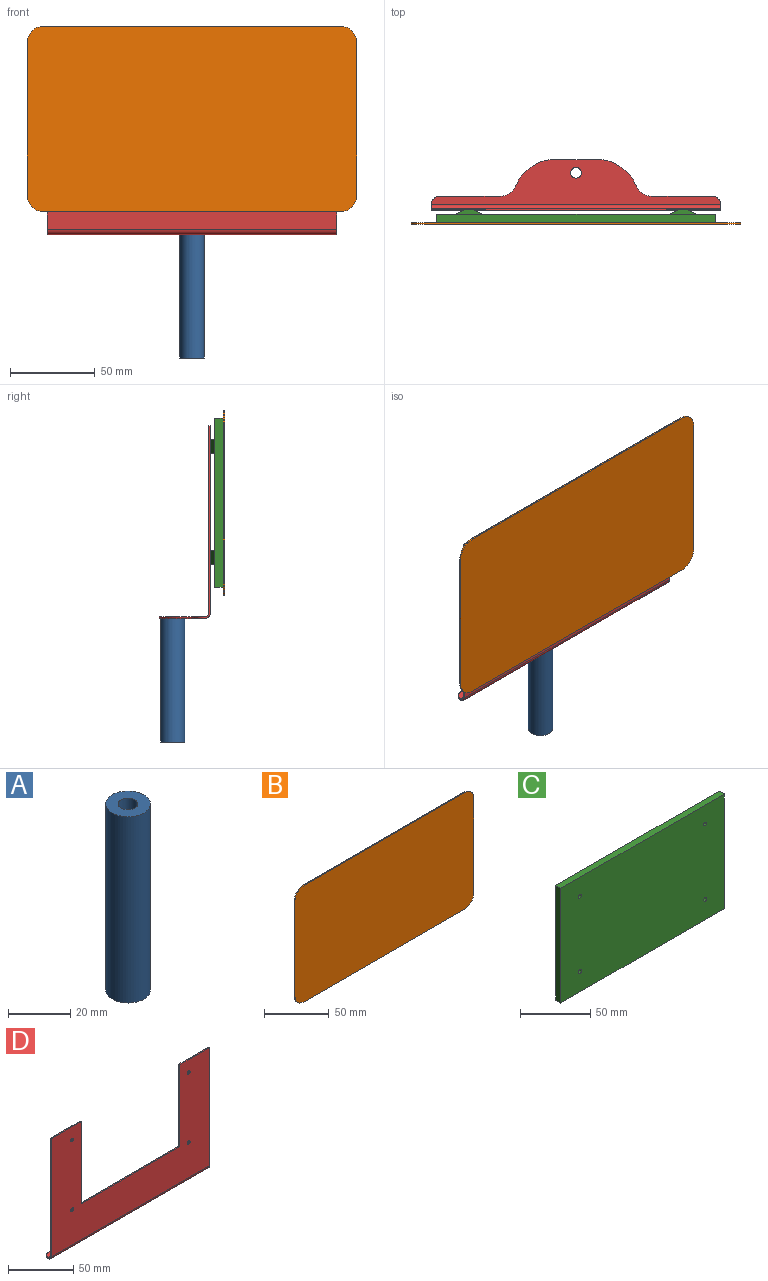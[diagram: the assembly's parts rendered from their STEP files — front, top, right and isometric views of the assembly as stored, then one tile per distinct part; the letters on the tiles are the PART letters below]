
ASSEMBLY  parts=4 mates=3
PART A: 4 faces, bbox 14.3x14.3x73 mm
  f0: cylinder r=3.17mm len=73mm, axis (0,0,1), area 1456.3mm2, adj f2,f3
  f1: cylinder r=7.15mm len=73mm, axis (0,0,1), area 3279.5mm2, adj f2,f3
  f2: plane 14.3x14.3mm, normal (0,0,-1), area 128.9mm2, adj f0,f1
  f3: plane 14.3x14.3mm, normal (0,0,1), area 128.9mm2, adj f0,f1
PART B: 10 faces, bbox 195x0.8x110 mm
  f0: plane 175x0.75mm, normal (0,0,-1), area 131.2mm2, adj f1,f7,f8,f9
  f1: cylinder r=10mm len=10mm, axis (0,1,0), area 11.8mm2, adj f0,f2,f8,f9
  f2: plane 90x0.75mm, normal (1,0,0), area 67.5mm2, adj f1,f3,f8,f9
  f3: cylinder r=10mm len=10mm, axis (0,1,0), area 11.8mm2, adj f2,f4,f8,f9
  f4: plane 175x0.75mm, normal (0,0,1), area 131.2mm2, adj f3,f5,f8,f9
  f5: cylinder r=10mm len=10mm, axis (0,1,0), area 11.8mm2, adj f4,f6,f8,f9
  f6: plane 90x0.75mm, normal (-1,0,0), area 67.5mm2, adj f5,f7,f8,f9
  f7: cylinder r=10mm len=10mm, axis (0,1,0), area 11.8mm2, adj f0,f6,f8,f9
  f8: plane 195x110mm, normal (0,-1,0), area 21364.2mm2, adj f0,f1,f2,f3,f4,f5,f6,f7
  f9: plane 195x110mm, normal (0,1,0), area 21364.2mm2, adj f0,f1,f2,f3,f4,f5,f6,f7
PART C: 30 faces, bbox 165x7.7x100 mm
  f0: plane 100x5.21mm, normal (-1,0,0), area 521mm2, adj f1,f6,f8,f9
  f1: plane 165x5.21mm, normal (0,0,-1), area 859.6mm2, adj f0,f2,f8,f9
  f2: plane 100x5.21mm, normal (1,0,0), area 521mm2, adj f1,f6,f8,f9
  f3: cylinder r=1.5mm len=7.71mm, axis (0,-1,0), area 72.7mm2, adj f9,f24
  f4: cylinder r=1.5mm len=7.71mm, axis (0,-1,0), area 72.7mm2, adj f9,f19
  f5: cylinder r=1.5mm len=7.71mm, axis (0,-1,0), area 72.7mm2, adj f9,f14
  f6: plane 165x5.21mm, normal (0,0,1), area 859.6mm2, adj f0,f2,f8,f9
  f7: cylinder r=1.5mm len=7.71mm, axis (0,-1,0), area 72.7mm2, adj f9,f29
  f8: plane 165x100mm, normal (0,1,0), area 15975.1mm2, adj f0,f1,f2,f6,f10,f11,f12,f13
  f9: plane 165x100mm, normal (0,-1,0), area 16471.7mm2, adj f0,f1,f2,f3,f4,f5,f6,f7
  f10: plane 8.15x5.36mm, normal (-0.42,0.91,0), area 48.2mm2, adj f8,f11,f13,f14
  f11: plane 16.1x2.5mm, normal (0,0,-1), area 26.8mm2, adj f8,f10,f12,f14
  f12: plane 8.15x5.36mm, normal (0.42,0.91,0), area 48.2mm2, adj f8,f11,f13,f14
  f13: plane 16.1x2.5mm, normal (0,0,1), area 26.8mm2, adj f8,f10,f12,f14
  f14: plane 8.15x5.38mm, normal (0,1,0), area 36.8mm2, adj f5,f10,f11,f12,f13
  f15: plane 8.15x5.36mm, normal (-0.42,0.91,0), area 48.2mm2, adj f8,f16,f18,f19
  f16: plane 16.1x2.5mm, normal (0,0,-1), area 26.8mm2, adj f8,f15,f17,f19
  f17: plane 8.15x5.36mm, normal (0.42,0.91,0), area 48.2mm2, adj f8,f16,f18,f19
  f18: plane 16.1x2.5mm, normal (0,0,1), area 26.8mm2, adj f8,f15,f17,f19
  f19: plane 8.15x5.38mm, normal (0,1,0), area 36.8mm2, adj f4,f15,f16,f17,f18
  f20: plane 8.15x5.36mm, normal (-0.42,0.91,0), area 48.2mm2, adj f8,f21,f23,f24
  f21: plane 16.1x2.5mm, normal (0,0,-1), area 26.8mm2, adj f8,f20,f22,f24
  f22: plane 8.15x5.36mm, normal (0.42,0.91,0), area 48.2mm2, adj f8,f21,f23,f24
  f23: plane 16.1x2.5mm, normal (0,0,1), area 26.8mm2, adj f8,f20,f22,f24
  f24: plane 8.15x5.38mm, normal (0,1,0), area 36.8mm2, adj f3,f20,f21,f22,f23
  f25: plane 8.15x5.36mm, normal (-0.42,0.91,0), area 48.2mm2, adj f8,f26,f28,f29
  f26: plane 16.1x2.5mm, normal (0,0,-1), area 26.8mm2, adj f8,f25,f27,f29
  f27: plane 8.15x5.36mm, normal (0.42,0.91,0), area 48.2mm2, adj f8,f26,f28,f29
  f28: plane 16.1x2.5mm, normal (0,0,1), area 26.8mm2, adj f8,f25,f27,f29
  f29: plane 8.15x5.38mm, normal (0,1,0), area 36.8mm2, adj f7,f25,f26,f27,f28
PART D: 31 faces, bbox 171.3x30x114.1 mm
  f0: plane 32.1x1mm, normal (0,0,1), area 32.1mm2, adj f1,f9,f11,f12
  f1: plane 110.84x1mm, normal (-1,0,0), area 110.8mm2, adj f0,f11,f12,f24
  f2: plane 110.84x1mm, normal (1,0,0), area 110.8mm2, adj f3,f11,f12,f23
  f3: plane 32.1x1mm, normal (0,0,1), area 32.1mm2, adj f2,f4,f11,f12
  f4: plane 77.03x1mm, normal (-1,0,0), area 77mm2, adj f3,f5,f11,f12
  f5: plane 107.11x1mm, normal (0,0,1), area 107.1mm2, adj f4,f9,f11,f12
  f6: cylinder r=1.55mm len=3.1mm, axis (0,1,0), area 9.7mm2, adj f11,f12
  f7: cylinder r=1.55mm len=3.1mm, axis (0,1,0), area 9.7mm2, adj f11,f12
  f8: cylinder r=1.55mm len=3.1mm, axis (0,1,0), area 9.7mm2, adj f11,f12
  f9: plane 77.03x1mm, normal (1,0,0), area 77mm2, adj f0,f5,f11,f12
  f10: cylinder r=1.55mm len=3.1mm, axis (0,1,0), area 9.7mm2, adj f11,f12
  f11: plane 171.31x110.84mm, normal (0,-1,0), area 10706.5mm2, adj f0,f1,f2,f3,f4,f5,f6,f7
  f12: plane 171.31x110.84mm, normal (0,1,0), area 10706.5mm2, adj f0,f1,f2,f3,f4,f5,f6,f7
  f13: plane 24.97x1mm, normal (0,1,0), area 25mm2, adj f21,f22,f27,f28
  f14: plane 1.22x1mm, normal (0.91,0.41,0), area 1.3mm2, adj f15,f21,f22,f27
  f15: cylinder r=10mm len=9.1mm, axis (0,0,-1), area 11.4mm2, adj f14,f16,f21,f22
  f16: plane 35.76x1mm, normal (0,1,0), area 35.8mm2, adj f15,f21,f22,f29
  f17: plane 35.76x1mm, normal (0,1,0), area 35.8mm2, adj f18,f21,f22,f30
  f18: cylinder r=10mm len=9.1mm, axis (0,0,-1), area 11.4mm2, adj f17,f20,f21,f22
  f19: cylinder r=3.17mm len=6.35mm, axis (0,0,-1), area 19.9mm2, adj f21,f22
  f20: plane 1.22x1mm, normal (-0.91,0.41,0), area 1.3mm2, adj f18,f21,f22,f28
  f21: plane 171.31x26.7mm, normal (0,0,-1), area 2191.9mm2, adj f13,f14,f15,f16,f17,f18,f19,f20
  f22: plane 171.31x26.7mm, normal (0,0,1), area 2191.9mm2, adj f13,f14,f15,f16,f17,f18,f19,f20
  f23: plane 3.3x3.29mm, normal (1,0,0), area 4.4mm2, adj f2,f25,f26,f29
  f24: plane 3.3x3.29mm, normal (-1,0,0), area 4.4mm2, adj f1,f25,f26,f30
  f25: cylinder r=3.3mm len=171.31mm, axis (1,0,0), area 888mm2, adj f11,f21,f23,f24,f29,f30
  f26: cylinder r=2.3mm len=171.31mm, axis (1,0,0), area 618.9mm2, adj f12,f22,f23,f24,f29,f30
  f27: cylinder r=25mm len=22.75mm, axis (0,0,1), area 28.6mm2, adj f13,f14,f21,f22
  f28: cylinder r=25mm len=22.75mm, axis (0,0,1), area 28.6mm2, adj f13,f20,f21,f22
  f29: cylinder r=5mm len=5mm, axis (0,0,1), area 7.9mm2, adj f16,f21,f22,f23,f25,f26
  f30: cylinder r=5mm len=5mm, axis (0,0,1), area 7.9mm2, adj f17,f21,f22,f24,f25,f26
PLACE A at identity
PLACE B at identity
PLACE C at identity
PLACE D at identity
MATE fastened D.f10 <-> C.f5  axis (0,-1,0) through (63.1,7.71,33.42)mm
MATE fastened D.f19 <-> A.f0  axis (0,0,-1) through (0,29.91,-68.41)mm
MATE fastened C.f9 <-> B.f9  axis (0,-1,0) through (0,0,0)mm
